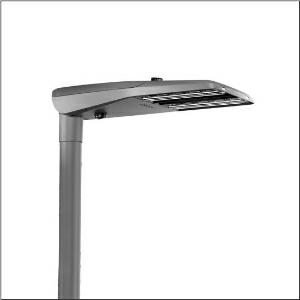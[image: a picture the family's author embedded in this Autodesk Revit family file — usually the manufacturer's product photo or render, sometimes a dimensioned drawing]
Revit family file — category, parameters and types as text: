
# Revit family: streetlight_sl_11_iq_midi___st1_2p1_0_5xc3g51y08me_d530
name_source: partatom
category: Lighting Fixtures
units: mm (PartAtom-declared; Revit-internal decimal feet)

## family parameters
Cut with Voids When Loaded = No
Host = Face
Light Source = No
Part Type = Normal
Room Calculation Point = No
Round Connector Dimension = Use Diameter
Shared = No

## types (1)
- --- (1 x LED, 17750 lm, 119.8 W, 3000K)
    Apparent Load = 120 VA
    CIE Flux Codes = 31 68 95 100 100
    Color Rendering = 70
    Color Temperature = 3000K
    Default Elevation = 1800 mm
    Description = Streetlight SL 11 iQ midi, mast luminaire, primary light control with 3 zone facetted reflector, of plastic, silver coated, highly specular, primary optical cover: cover, of PMMA, transparent, light distribution: ST1.2P1.0, light emission: direct distribution, primary light characteristic: asymmetric, installation type: post-top, side-entry, lamps: LED, High Power LED, rated values: 17.750lm | 119,8W | 148,2lm/W (begin service life); end service life: 17.750lm | 126,7W; at 50% lumin. flux: 8.875lm | 54,9W | 161,7lm/W, colour temperature: 3000K, colour rendering: CRI > 70, light colour: 730, light setting 1 begin service life: 100% | 17.750lm | 119,8W | 148,2lm/W | 3.000K, light setting 1 end service life: 126,7W, further light settings possible, control: pre-setting: logarithmic dimming characteristic, Street-Remote, Auto-Match, Temp-Guard, Lumen-Switch, Night-Set, Smart-Wire, Light-Fading, Desk-Remote (wireless, voltage-free reading and setting of iQ features in the workshop via application-optimized NFC function/RFID function), optimised constant luminous flux control (CLO 2.0), with cable H07RN-F 5x 1.5mm², mains connection: 230..240V, AC, 50/60Hz, connection cable pre-assembled, cable length: 12,5m, luminaire housing, of diecast aluminium, powder-coated, Siteco® metallic grey (DB 702S), please order mast flange separately, inclination adjustable without tools: 0°, 5°, 10°, 15° (post-top) | 0°, -5°, -10°, -15° (side-entry), sealing non-destructively replaceable, multi-level sealing system, length: 780mm, width: 376mm, height: 118mm, mast flange for spigot size: 42mm (side-entry): 5XC10008XM4, 60/48mm (side-entry/post-top): 5XC10108XM2, 76/60mm (side-entry/post-top): 5XC10108XM1, equipment: Power, Smart Interface below and above, protection rating (complete): IP66, insulation class (complete): insulation class II (safety insulation), certification: CE, ENEC, ENEC+, VDE, UKCA, impact resistance: IK10, permissible operating ambient temperature for outdoor applications: -25..+50°C, standard-compliant lighting for roads and squares, Environmental Product Declaration (EPD) tested and certified by an independent institute, packaging unit: 1 piece

Light Distribution: ST1.2P1.0
    Height = 118 mm
    Lamp = 1 x LED
    Lamp Light Flux = 17750 lm
    Lamp Power = 119.8 W
    Lamp count = 1
    Length = 780 mm
    Luminous efficacy = 148 lm/W
    Manufacturer = Siteco
    ModVariant = No
    Model = 5XC3G51Y08ME
    Number of Poles = 1
    OnlyDefault = Yes
    Power Factor = 1
    Product Name = Streetlight SL 11 iQ midi | ST1.2P1.0
    Product group = mast luminaire | pylon top
    ProductGroupID = 6100
    Protection Class = Protection class II
    Protection Degree = IP 66
    RLX_Detail_Level = 1
    RLX_Emergency_Light_Flux = 0 lm
    RLX_Emergency_Type = 0
    RLX_Emergency_Type_DB = No
    RlxData = <blob elided: 69957 chars, md5=a2207f30>
    Socket = socket
    Standby Power = 0 W
    System Light Flux = 17750 lm
    System Power = 120 W
    Type Comments = factory setting: luminous flux: 100 % | dim-lin: 254 | 540 mA
    Type Image = l_1004429.jpg
    URL = http://relux.com
    VarID = @adj_057491
    Voltage = 0 V
    Weight = 0.00 kg
    Width = 376 mm

## geometry (parser evidence)
native form markers: Blend x4, Sweep x9
no freeform markers — native parametric forms only
